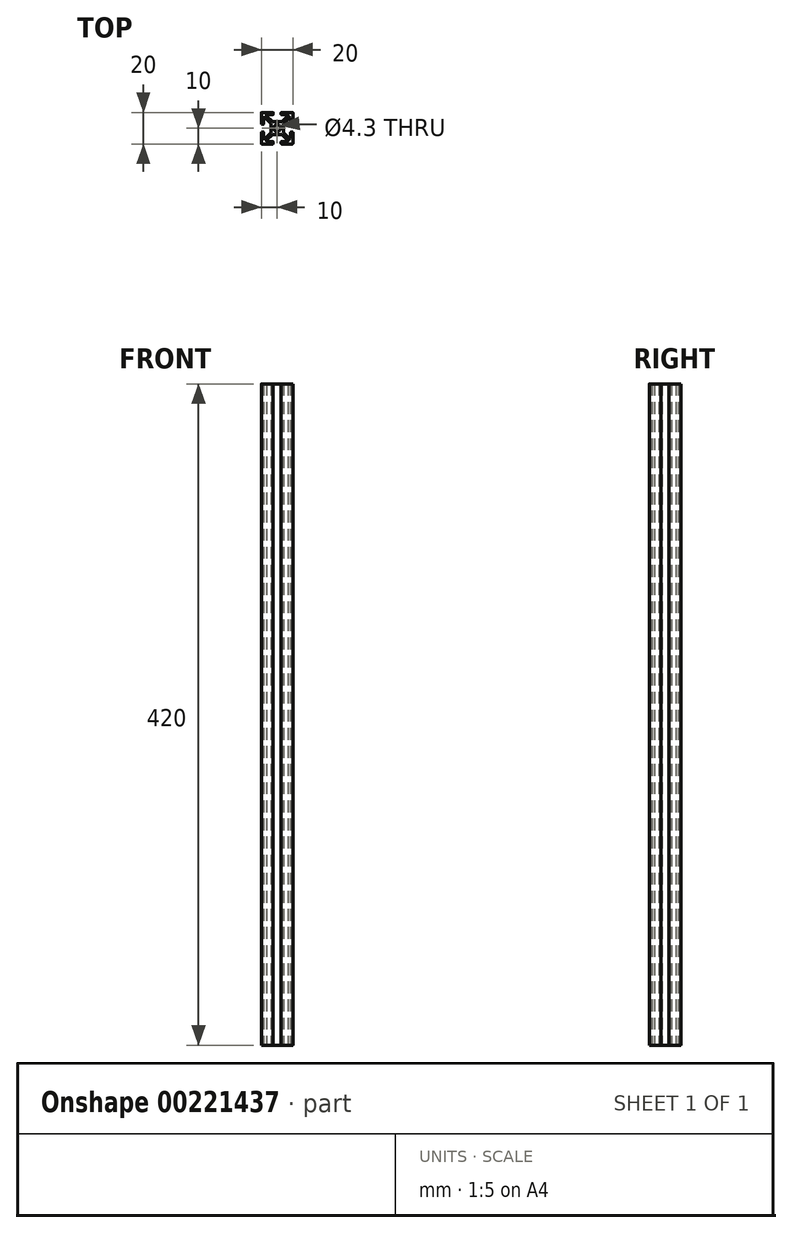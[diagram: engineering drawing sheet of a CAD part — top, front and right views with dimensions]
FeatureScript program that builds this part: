
annotation { "Feature Type Name" : "Feature", "Feature Type Description" : "" }
export const myFeature = defineFeature(function(context is Context, id is Id, definition is map)
    precondition{}
    {
        {
            var Q0;
            Q0=qCreatedBy(makeId("Top.planeOp"),FACE);
            var sketch = newSketch(context, id + "F0", { "sketchPlane" : qUnion([Q0])});
            skLineSegment(sketch, "E0.bottom", {"start": v(0, 0) * mm, "end": v(20, 0) * mm, "construction": true});
            skLineSegment(sketch, "E0.top", {"start": v(0, -20) * mm, "end": v(20, -20) * mm, "construction": true});
            skLineSegment(sketch, "E0.left", {"start": v(0, 0) * mm, "end": v(0, -20) * mm, "construction": true});
            skLineSegment(sketch, "E0.right", {"start": v(20, 0) * mm, "end": v(20, -20) * mm, "construction": true});
            skCircle(sketch, "E1", {"center": v(10, -10) * mm, "radius": 2.15 * mm});
            skPoint(sketch, "E1.centerSnap0", {"position": v(10, 0) * mm});
            skPoint(sketch, "E1.centerSnap1", {"position": v(0, -10) * mm});
            skLineSegment(sketch, "E2.bottom", {"start": v(6, -6) * mm, "end": v(14, -6) * mm, "construction": true});
            skLineSegment(sketch, "E2.top", {"start": v(6, -14) * mm, "end": v(14, -14) * mm, "construction": true});
            skLineSegment(sketch, "E2.left", {"start": v(6, -6) * mm, "end": v(6, -14) * mm, "construction": true});
            skLineSegment(sketch, "E2.right", {"start": v(14, -6) * mm, "end": v(14, -14) * mm, "construction": true});
            skLineSegment(sketch, "E3", {"start": v(19.8, 0) * mm, "end": v(12.7, 0) * mm});
            skLineSegment(sketch, "E4.0", {"start": v(16.55, -1.5) * mm, "end": v(12.7, -1.5) * mm});
            skLineSegment(sketch, "E5", {"start": v(14, -6) * mm, "end": v(20, 0) * mm, "construction": true});
            skLineSegment(sketch, "E6.0", {"start": v(14, -7.06) * mm, "end": v(17.75, -3.3) * mm});
            skLineSegment(sketch, "E7.0", {"start": v(12.94, -6) * mm, "end": v(16.7, -2.25) * mm});
            skLineSegment(sketch, "E8", {"start": v(20, -0.2) * mm, "end": v(20, -7.3) * mm});
            skLineSegment(sketch, "E9.0", {"start": v(18.5, -3.45) * mm, "end": v(18.5, -7.3) * mm});
            skLineSegment(sketch, "E10", {"start": v(18.3, -3.25) * mm, "end": v(17.9, -3.25) * mm});
            skLineSegment(sketch, "E11", {"start": v(16.75, -1.7) * mm, "end": v(16.75, -2.1) * mm});
            skLineSegment(sketch, "E12", {"start": v(12.5, -0.2) * mm, "end": v(12.5, -1.3) * mm});
            skLineSegment(sketch, "E13", {"start": v(18.7, -7.5) * mm, "end": v(19.8, -7.5) * mm});
            skLineSegment(sketch, "E14", {"start": v(10, -10) * mm, "end": v(20, -10) * mm, "construction": true});
            skLineSegment(sketch, "E15", {"start": v(10, -10) * mm, "end": v(10, 0) * mm, "construction": true});
            skPoint(sketch, "E16.visualSharp", {"position": v(20, 0) * mm});
            skArc(sketch, "E16.filletArc", {"start": v(20, -0.2) * mm, "mid": v(19.94, -0.06) * mm, "end": v(19.8, 0) * mm});
            skPoint(sketch, "E17.visualSharp", {"position": v(12.5, 0) * mm});
            skArc(sketch, "E17.filletArc", {"start": v(12.7, 0) * mm, "mid": v(12.56, -0.06) * mm, "end": v(12.5, -0.2) * mm});
            skPoint(sketch, "E18.visualSharp", {"position": v(12.5, -1.5) * mm});
            skArc(sketch, "E18.filletArc", {"start": v(12.5, -1.3) * mm, "mid": v(12.56, -1.44) * mm, "end": v(12.7, -1.5) * mm});
            skPoint(sketch, "E19.visualSharp", {"position": v(18.5, -7.5) * mm});
            skArc(sketch, "E19.filletArc", {"start": v(18.5, -7.3) * mm, "mid": v(18.56, -7.44) * mm, "end": v(18.7, -7.5) * mm});
            skPoint(sketch, "E20.visualSharp", {"position": v(20, -7.5) * mm});
            skArc(sketch, "E20.filletArc", {"start": v(19.8, -7.5) * mm, "mid": v(19.94, -7.44) * mm, "end": v(20, -7.3) * mm});
            skPoint(sketch, "E21.visualSharp", {"position": v(16.75, -1.5) * mm});
            skArc(sketch, "E21.filletArc", {"start": v(16.75, -1.7) * mm, "mid": v(16.7, -1.56) * mm, "end": v(16.55, -1.5) * mm});
            skPoint(sketch, "E22.visualSharp", {"position": v(16.75, -2.19) * mm});
            skArc(sketch, "E22.filletArc", {"start": v(16.7, -2.25) * mm, "mid": v(16.73, -2.18) * mm, "end": v(16.75, -2.1) * mm});
            skPoint(sketch, "E23.visualSharp", {"position": v(17.81, -3.25) * mm});
            skArc(sketch, "E23.filletArc", {"start": v(17.9, -3.25) * mm, "mid": v(17.82, -3.27) * mm, "end": v(17.75, -3.3) * mm});
            skPoint(sketch, "E24.visualSharp", {"position": v(18.5, -3.25) * mm});
            skArc(sketch, "E24.filletArc", {"start": v(18.5, -3.45) * mm, "mid": v(18.44, -3.3) * mm, "end": v(18.3, -3.25) * mm});
            skLineSegment(sketch, "E25.MirrorCS", {"start": v(14, -12.94) * mm, "end": v(17.75, -16.7) * mm});
            skArc(sketch, "E26.MirrorCS", {"start": v(17.9, -16.75) * mm, "mid": v(17.82, -16.73) * mm, "end": v(17.75, -16.7) * mm});
            skLineSegment(sketch, "E27.MirrorCS", {"start": v(18.3, -16.75) * mm, "end": v(17.9, -16.75) * mm});
            skArc(sketch, "E28.MirrorCS", {"start": v(18.5, -16.55) * mm, "mid": v(18.44, -16.7) * mm, "end": v(18.3, -16.75) * mm});
            skLineSegment(sketch, "E29.MirrorCS", {"start": v(18.5, -16.55) * mm, "end": v(18.5, -12.7) * mm});
            skArc(sketch, "E30.MirrorCS", {"start": v(18.5, -12.7) * mm, "mid": v(18.56, -12.56) * mm, "end": v(18.7, -12.5) * mm});
            skLineSegment(sketch, "E31.MirrorCS", {"start": v(18.7, -12.5) * mm, "end": v(19.8, -12.5) * mm});
            skArc(sketch, "E32.MirrorCS", {"start": v(19.8, -12.5) * mm, "mid": v(19.94, -12.56) * mm, "end": v(20, -12.7) * mm});
            skLineSegment(sketch, "E33.MirrorCS", {"start": v(20, -19.8) * mm, "end": v(20, -12.7) * mm});
            skArc(sketch, "E34.MirrorCS", {"start": v(20, -19.8) * mm, "mid": v(19.94, -19.94) * mm, "end": v(19.8, -20) * mm});
            skLineSegment(sketch, "E35.MirrorCS", {"start": v(19.8, -20) * mm, "end": v(12.7, -20) * mm});
            skArc(sketch, "E36.MirrorCS", {"start": v(12.7, -20) * mm, "mid": v(12.56, -19.94) * mm, "end": v(12.5, -19.8) * mm});
            skLineSegment(sketch, "E37.MirrorCS", {"start": v(12.5, -19.8) * mm, "end": v(12.5, -18.7) * mm});
            skArc(sketch, "E38.MirrorCS", {"start": v(12.5, -18.7) * mm, "mid": v(12.56, -18.56) * mm, "end": v(12.7, -18.5) * mm});
            skLineSegment(sketch, "E39.MirrorCS", {"start": v(16.55, -18.5) * mm, "end": v(12.7, -18.5) * mm});
            skArc(sketch, "E40.MirrorCS", {"start": v(16.75, -18.3) * mm, "mid": v(16.7, -18.44) * mm, "end": v(16.55, -18.5) * mm});
            skLineSegment(sketch, "E41.MirrorCS", {"start": v(16.75, -18.3) * mm, "end": v(16.75, -17.9) * mm});
            skArc(sketch, "E42.MirrorCS", {"start": v(16.7, -17.75) * mm, "mid": v(16.73, -17.82) * mm, "end": v(16.75, -17.9) * mm});
            skLineSegment(sketch, "E43.MirrorCS", {"start": v(12.94, -14) * mm, "end": v(16.7, -17.75) * mm});
            skArc(sketch, "E44.MirrorCS", {"start": v(0, -0.2) * mm, "mid": v(0.06, -0.06) * mm, "end": v(0.2, 0) * mm});
            skLineSegment(sketch, "E45.MirrorCS", {"start": v(3.25, -1.7) * mm, "end": v(3.25, -2.1) * mm});
            skArc(sketch, "E46.MirrorCS", {"start": v(1.5, -3.45) * mm, "mid": v(1.56, -3.3) * mm, "end": v(1.7, -3.25) * mm});
            skArc(sketch, "E47.MirrorCS", {"start": v(3.25, -1.7) * mm, "mid": v(3.3, -1.56) * mm, "end": v(3.45, -1.5) * mm});
            skArc(sketch, "E48.MirrorCS", {"start": v(3.3, -2.25) * mm, "mid": v(3.27, -2.18) * mm, "end": v(3.25, -2.1) * mm});
            skArc(sketch, "E49.MirrorCS", {"start": v(1.5, -7.3) * mm, "mid": v(1.44, -7.44) * mm, "end": v(1.3, -7.5) * mm});
            skArc(sketch, "E50.MirrorCS", {"start": v(2.1, -3.25) * mm, "mid": v(2.18, -3.27) * mm, "end": v(2.25, -3.3) * mm});
            skArc(sketch, "E51.MirrorCS", {"start": v(0.2, -7.5) * mm, "mid": v(0.06, -7.44) * mm, "end": v(0, -7.3) * mm});
            skLineSegment(sketch, "E52.MirrorCS", {"start": v(1.7, -3.25) * mm, "end": v(2.1, -3.25) * mm});
            skArc(sketch, "E53.MirrorCS", {"start": v(1.5, -16.55) * mm, "mid": v(1.56, -16.7) * mm, "end": v(1.7, -16.75) * mm});
            skArc(sketch, "E54.MirrorCS", {"start": v(7.5, -1.3) * mm, "mid": v(7.44, -1.44) * mm, "end": v(7.3, -1.5) * mm});
            skLineSegment(sketch, "E55.MirrorCS", {"start": v(1.7, -16.75) * mm, "end": v(2.1, -16.75) * mm});
            skArc(sketch, "E56.MirrorCS", {"start": v(3.25, -18.3) * mm, "mid": v(3.3, -18.44) * mm, "end": v(3.45, -18.5) * mm});
            skLineSegment(sketch, "E57.MirrorCS", {"start": v(3.25, -18.3) * mm, "end": v(3.25, -17.9) * mm});
            skArc(sketch, "E58.MirrorCS", {"start": v(0, -19.8) * mm, "mid": v(0.06, -19.94) * mm, "end": v(0.2, -20) * mm});
            skArc(sketch, "E59.MirrorCS", {"start": v(0.2, -12.5) * mm, "mid": v(0.06, -12.56) * mm, "end": v(0, -12.7) * mm});
            skArc(sketch, "E60.MirrorCS", {"start": v(3.3, -17.75) * mm, "mid": v(3.27, -17.82) * mm, "end": v(3.25, -17.9) * mm});
            skArc(sketch, "E61.MirrorCS", {"start": v(7.3, -20) * mm, "mid": v(7.44, -19.94) * mm, "end": v(7.5, -19.8) * mm});
            skArc(sketch, "E62.MirrorCS", {"start": v(1.5, -12.7) * mm, "mid": v(1.44, -12.56) * mm, "end": v(1.3, -12.5) * mm});
            skArc(sketch, "E63.MirrorCS", {"start": v(2.1, -16.75) * mm, "mid": v(2.18, -16.73) * mm, "end": v(2.25, -16.7) * mm});
            skArc(sketch, "E64.MirrorCS", {"start": v(7.5, -18.7) * mm, "mid": v(7.44, -18.56) * mm, "end": v(7.3, -18.5) * mm});
            skArc(sketch, "E65.MirrorCS", {"start": v(7.3, 0) * mm, "mid": v(7.44, -0.06) * mm, "end": v(7.5, -0.2) * mm});
            skLineSegment(sketch, "E66.MirrorCS", {"start": v(1.3, -7.5) * mm, "end": v(0.2, -7.5) * mm});
            skPoint(sketch, "E67.MirrorP", {"position": v(7.5, -1.5) * mm});
            skLineSegment(sketch, "E68.MirrorCS", {"start": v(7.5, -0.2) * mm, "end": v(7.5, -1.3) * mm});
            skPoint(sketch, "E69.MirrorP", {"position": v(3.25, -1.5) * mm});
            skLineSegment(sketch, "E70.MirrorCS", {"start": v(7.06, -14) * mm, "end": v(3.3, -17.75) * mm});
            skLineSegment(sketch, "E71.MirrorCS", {"start": v(1.3, -12.5) * mm, "end": v(0.2, -12.5) * mm});
            skLineSegment(sketch, "E72.MirrorCS", {"start": v(7.06, -6) * mm, "end": v(3.3, -2.25) * mm});
            skLineSegment(sketch, "E73.MirrorCS", {"start": v(1.5, -16.55) * mm, "end": v(1.5, -12.7) * mm});
            skLineSegment(sketch, "E74.MirrorCS", {"start": v(0, -0.2) * mm, "end": v(0, -7.3) * mm});
            skLineSegment(sketch, "E75.MirrorCS", {"start": v(0.2, -20) * mm, "end": v(7.3, -20) * mm});
            skLineSegment(sketch, "E76.MirrorCS", {"start": v(0.2, 0) * mm, "end": v(7.3, 0) * mm});
            skLineSegment(sketch, "E77.MirrorCS", {"start": v(7.5, -19.8) * mm, "end": v(7.5, -18.7) * mm});
            skLineSegment(sketch, "E78.MirrorCS", {"start": v(1.5, -3.45) * mm, "end": v(1.5, -7.3) * mm});
            skPoint(sketch, "E79.MirrorP", {"position": v(0, 0) * mm});
            skPoint(sketch, "E80.MirrorP", {"position": v(1.5, -3.25) * mm});
            skLineSegment(sketch, "E81.MirrorCS", {"start": v(3.45, -1.5) * mm, "end": v(7.3, -1.5) * mm});
            skLineSegment(sketch, "E82.MirrorCS", {"start": v(6, -12.94) * mm, "end": v(2.25, -16.7) * mm});
            skPoint(sketch, "E83.MirrorP", {"position": v(2.19, -3.25) * mm});
            skLineSegment(sketch, "E84.MirrorCS", {"start": v(0, -19.8) * mm, "end": v(0, -12.7) * mm});
            skLineSegment(sketch, "E85.MirrorCS", {"start": v(3.45, -18.5) * mm, "end": v(7.3, -18.5) * mm});
            skPoint(sketch, "E86.MirrorP", {"position": v(1.5, -7.5) * mm});
            skLineSegment(sketch, "E87.MirrorCS", {"start": v(6, -7.06) * mm, "end": v(2.25, -3.3) * mm});
            skLineSegment(sketch, "E88.MirrorCS", {"start": v(6, -6) * mm, "end": v(0, 0) * mm, "construction": true});
            skPoint(sketch, "E89.MirrorP", {"position": v(0, -7.5) * mm});
            skPoint(sketch, "E90.MirrorP", {"position": v(3.25, -2.19) * mm});
            skPoint(sketch, "E91.MirrorP", {"position": v(7.5, 0) * mm});
            skLineSegment(sketch, "E92", {"start": v(7.06, -6) * mm, "end": v(12.94, -6) * mm});
            skLineSegment(sketch, "E93", {"start": v(14, -7.06) * mm, "end": v(14, -12.94) * mm});
            skLineSegment(sketch, "E94", {"start": v(12.94, -14) * mm, "end": v(7.06, -14) * mm});
            skLineSegment(sketch, "E95", {"start": v(6, -12.94) * mm, "end": v(6, -7.06) * mm});
            skSolve(sketch);
        }
        {
            var Q0;
            Q0=makeQuery(id+"F0.imprint","IMPRINT",FACE,{"disambiguationData":[TD([[makeQuery(id+"F0.imprint","IMPRINT",EDGE,{"derivedFrom":sQuery(id+"F0.wireOp",EDGE,"E1")}),-1.0]])]});
            extrude(context, id + "F1", {"entities" : qUnion([Q0]), "depth" : 420 * mm});
        }
    });
